# Revit family: 05_MAGIS40-33_FIX
name_source: partatom
category: Finestre
units: mm (PartAtom-declared; Revit-internal decimal feet)

## family parameters
Condiviso = No
Host = Muro
Numero OmniClass = 23.30.20.00
Punto di calcolo locali = Sì
Sempre verticale = Sì
Taglio con vuoti quando caricato = No
Titolo OmniClass = Windows

## types (3) — shared parameters
Altezza di default del davanzale = 800 mm
Chiusura muro = Per host
Costruzione analitica = <Nessuno>
EXTERNAL ALUMINUM FRAME/TELAIO ALLUMINIO ESTERNO = UNIFORM_ALUMINUM
GLASS WEIGHT/PESO VETRO = 30.00 kg/m²
HANDLE/MANIGLIA = UNIFORM_ALUMINUM
INTERIOR WOOD FRAME/TELAIO LEGNO INTERNO = UNIFORM_WOOD
MAX_DIMENSIONS_WARNING = No
MINIMUM HEIGHT/ALTEZZA MINIMA = 400 mm
MINIMUM WIDTH/LARGHEZZA MINIMA  = 400 mm
Modello = MAGIS40
PRODUCER WEBSITE/SITO WEB PRODUTTORE = www.uniform.it
WINDOW GLASS/VETRO FINESTRA = UNIFORM_GLASS

## per-type parameters (varying)
| type | Altezza | H | HANDLE HEIGHT/ALTEZZA MANIGLIA | Larghezza | MAXIMUM HEIGHT/ALTEZZA MASSIMA | MAXIMUM WIDTH/LARGHEZZA MASSIMA | PRODUCT WEBSITE/SITO WEB PRODOTTO | Rw GLASS/Rw VETRO | Rw WINDOW/Rw FINESTRA | Ug GLASS/Ug VETRO | Uw WINDOW/Uw FINESTRA | W |
| ACOUSTICS | 1600 mm | 1600 mm | 800 mm | 1000 mm  [stored 3.28084 ft] | 2000 mm  [stored 6.56168 ft] | 1200 mm  [stored 3.93701 ft] | www.sistema-uni-one.it | 43 | 40 | 1.6 W/(m²·K) | 1.6 W/(m²·K) | 1000 mm  [stored 3.28084 ft] |
| THERMAL_PERFORMANCE | 2000 mm  [stored 6.56168 ft] | 2000 mm  [stored 6.56168 ft] | 500 mm | 1000 mm  [stored 3.28084 ft] | 3000 mm | 3500 mm |  | 0 | 0 | 0.5 W/(m²·K) | 1.1 W/(m²·K) | 1000 mm  [stored 3.28084 ft] |
| THERMAL | 2000 mm  [stored 6.56168 ft] | 2000 mm  [stored 6.56168 ft] | 500 mm | 1200 mm  [stored 3.93701 ft] | 3000 mm | 3500 mm | www.sistema-uni-one.it | 0 | 0 | 1 W/(m²·K) | 1.4 W/(m²·K) | 1200 mm  [stored 3.93701 ft] |

note: [stored X ft] marks values corroborated as IEEE doubles in the binary element streams (Revit-internal decimal feet)
